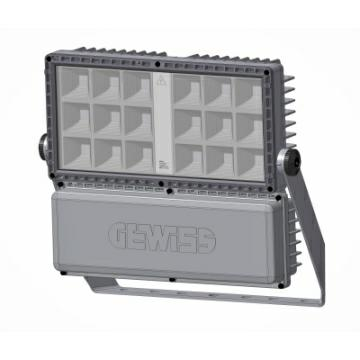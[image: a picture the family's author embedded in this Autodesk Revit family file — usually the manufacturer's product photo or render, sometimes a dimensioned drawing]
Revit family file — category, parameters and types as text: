
# Revit family: Lighting-Floodlights-GEWISS-SMART[PRO]2.0-LED-MEDIUM-POWER_1MODULE_DALI.CLII
name_source: partatom
category: Apparecchi per illuminazione
units: mm (PartAtom-declared; Revit-internal decimal feet)

## family parameters
Condiviso = No
Host = Superficie
Punto di calcolo locali = No
Quota connettore circolare = Usa diametro
Sorgente d'illuminazione = No
Taglio con vuoti quando caricato = No
Tipo di parte = Normale

## types (45) — shared parameters
Applicazione = Indoor / Outdoor
Body = Die-cast aluminium -
Catalogue = LIGHTING
Classification: = -
Colour = Graphite grey
Colour : = Polyester powder coated
Context = Sport, Big Areas
Control System = DALI
DIN 18032-3 certification = Yes
Device with reduced surface temperature = Yes
Driver = Included
Driver Box = Built-in
Eletrical and lighting features = -
External screw = Stainless steel
Fixing = Bracket
GW - Codice Electrocod = 2424
Gasket = Anti-aging silicone
General information = -
Glow Wire Test : = -
IDF = d05ed8b5-b81d-4cb0-8872-352464a63a3f
IDT = 44936a2a5e034791af2c92c80339c9aa
IP degree = IP66
Immagine tipo = SMARTPRO20_1M.jpg
Installationa and maintenance = -
Insulation class = II
LED Maintenance = Not available
Lifetime = L90B10 (Tq+25°C) - 50000h L90B10 (Tq+50°C) = 32000h L80B10 (Tq+25°C) - 110000h
Locking Hook = Hexagonal metric screws
Luminaire = LED luminaire with small,mid and high lumen power
Materials = -
Maximum surface exposed to the wind : = 0,085 m2
Mouting and installation = High-mast lighting - Wall mounting - Ground mouting
Operating temperature : = -30 +50 °C
Optic Maintenance = Not available
Optic and illuminating features = -
Overvoltage protection = DM 6 kV / CM 10 kV
Photobiological Risk Class = -
Produttore = GEWISS S.p.A.
Prospetto di default = 1219 mm
Rated frequency (Hz) = 50 / 60
SEO = Floodlight
Shield type = Flat tempered glass 4mm
Shock resistance = IK08
Standard- = EN60598-1; EN60598-2-5; EN60598-2-24; IEC 62778; IEC62471; EN13201
Standards and approvals = -
Stocking temperature = -
Supply voltage = 220 - 240 V
System power = 165W
Technical sheet = https://www.gewiss.com
Tilt- = Rotation on bracket with integrated goniometer
Type of light source = LED - Not replaceable
URL = https://www.gewiss.com
Unique digital code (Datamatrix) = Currently not present
Version file RFA = 20.11
Warranty = 5 years
Weight (kg): = 5,7
Wiring = Watertight connector

## per-type parameters (varying)
| type | Color Rendering Index | Colour temperature | Descrizione | Efficiency (lm/W) | IPEA | Lumen output (lm) | Modello | Optic | Optic : | Standard Deviation Colour Matching | Unified Glare Rating | Versions |
| GWP2174LB - SMARTPRO2.0 1M 4000K CRI70 C2 DALI CL2 | CRI-70 | 4000K | SMARTPRO2.0 1M 4000K CRI70 C2 DALI CL2 | 121 | ROAD = A ++ // LARGE AREAS = A5 + // CYCLOPEDONALS = A ++ // GREEN AREAS = A ++ // HISTORICAL CENTER = A7 + // OTHER = A7 + | 20000 | GWP2174LB | C2 - Circular 25° | Polished quartz and metallized PC HT reflector | SDCM = 5 | G*6 - ULOR = 0 | 4000K natural light |
| GWP2183BB - SMARTPRO2.0 1M 3000K CRI80 S2 DALI CL2 | CRI-80 | 3000K | SMARTPRO2.0 1M 3000K CRI80 S2 DALI CL2 | 107 | ROAD = A // LARGE AREAS = A3 + // CYCLOPEDONALS = A + // GREEN AREAS = A + // HISTORICAL CENTER = A5 + // OTHER = A5 + | 17600 | GWP2183BB | S2 - Symmetric Medium | Polished anodised aluminum reflector with 99.99% pure aluminum | SDCM = 3 | G*6 - ULOR = 0 | 3000K warm light |
| GWP2174CB - SMARTPRO2.0 1M 4000K CRI70 A1 DALI CL2 | CRI-70 | 4000K | SMARTPRO2.0 1M 4000K CRI70 A1 DALI CL2 | 116 | ROAD = A + // LARGE AREAS = A5 + // CYCLOPEDONALS = A ++ // GREEN AREAS = A ++ // HISTORICAL CENTER = A6 + // OTHER = A6 + | 19100 | GWP2174CB | A1 - Asymmetrical Wide | Polished quartz and metallized PC HT reflector | SDCM = 5 | G*4 - ULOR = 0 | 4000K natural light |
| GWP2184MB - SMARTPRO2.0 1M 4000K CRI80 C1 DALI CL2 | CRI-80 | 4000K | SMARTPRO2.0 1M 4000K CRI80 C1 DALI CL2 | 113 | - | 18700 | GWP2184MB | C1 - Circular 30° | Polished quartz and metallized PC HT reflector | SDCM = 3 | G*6 - ULOR = 0 | 4000K natural light |
| GWP2174GB - SMARTPRO2.0 1M 4000K CRI70 C4 DALI CL2 | CRI-70 | 4000K | SMARTPRO2.0 1M 4000K CRI70 C4 DALI CL2 | 124 | ROAD = A ++ // LARGE AREAS = A6 + // CYCLOPEDONALS = A3 + // GREEN AREAS = A3 + // HISTORICAL CENTER = A8 + // OTHER = A8 + | 20500 | GWP2174GB | C4 - Circular 15° | Polished quartz and metallized PC HT reflector | SDCM = 5 | G*6 - ULOR = 0 | 4000K natural light |
| GWP2173FB - SMARTPRO2.0 1M 3000K CRI70 A2 DALI CL2 | CRI-70 | 3000K | SMARTPRO2.0 1M 3000K CRI70 A2 DALI CL2 | 93 | ROAD = B // LARGE AREAS = A + // CYCLOPEDONALS = B // GREEN AREAS = B // HISTORICAL CENTER = A3 + // OTHER = A3 + | 15300 | GWP2173FB | A2 - Asymmetrical Medium | Polished anodised aluminum reflector with 99.99% pure aluminum | SDCM = 5 | G*3 - ULOR = 0 | 3000K warm light |
| GWP2174BB - SMARTPRO2.0 1M 4000K CRI70 S2 DALI CL2 | CRI-70 | 4000K | SMARTPRO2.0 1M 4000K CRI70 S2 DALI CL2 | 123 | ROAD = A ++ // LARGE AREAS = A6 + // CYCLOPEDONALS = A3 + // GREEN AREAS = A3 + // HISTORICAL CENTER = A7 + // OTHER = A7 + | 20300 | GWP2174BB | S2 - Symmetric Medium | Polished anodised aluminum reflector with 99.99% pure aluminum | SDCM = 5 | G*6 - ULOR = 0 | 4000K natural light |
| GWP2175LB - SMARTPRO2.0 1M 5700K CRI70 C2 DALI CL2 | CRI-70 | 5700K | SMARTPRO2.0 1M 5700K CRI70 C2 DALI CL2 | 121 | ROAD = A ++ // LARGE AREAS = A5 + // CYCLOPEDONALS = A ++ // GREEN AREAS = A ++ // HISTORICAL CENTER = A7 + // OTHER = A7 + | 20000 | GWP2175LB | C2 - Circular 25° | Polished quartz and metallized PC HT reflector | SDCM = 5 | G*6 - ULOR = 0 | 5700K cold light |
| GWP2183MB - SMARTPRO2.0 1M 3000K CRI80 C1 DALI CL2 | CRI-80 | 3000K | SMARTPRO2.0 1M 3000K CRI80 C1 DALI CL2 | 105 | ROAD = A // LARGE AREAS = A3 + // CYCLOPEDONALS = A + // GREEN AREAS = A + // HISTORICAL CENTER = A5 + // OTHER = A5 + | 17400 | GWP2183MB | C1 - Circular 30° | Polished quartz and metallized PC HT reflector | SDCM = 3 | G*6 - ULOR = 0 | 3000K warm light |
| GWP2175NB - SMARTPRO2.0 1M 5700K CRI70 A3 DALI CL2 | CRI-70 | 5700K | SMARTPRO2.0 1M 5700K CRI70 A3 DALI CL2 | 114 | - | 18800 | GWP2175NB | A3 - Assymetric Narrow | Polished anodised aluminum reflector with 99.99% pure aluminum | SDCM = 5 | G*6 - ULOR = 0 | 5700K cold light |
| GWP2174AB - SMARTPRO2.0 1M 4000K CRI70 S1 DALI CL2 | CRI-70 | 4000K | SMARTPRO2.0 1M 4000K CRI70 S1 DALI CL2 | 119 | ROAD = A ++ // LARGE AREAS = A5 + // CYCLOPEDONALS = A ++ // GREEN AREAS = A ++ // HISTORICAL CENTER = A7 + // OTHER = A7 + | 19600 | GWP2174AB | S1 - Symmetric Wide | Polished quartz and metallized PC HT reflector | SDCM = 5 | G*6 - ULOR = 0 | 4000K natural light |
| GWP2184HB - SMARTPRO2.0 1M 4000K CRI80 C3 DALI CL2 | CRI-80 | 4000K | SMARTPRO2.0 1M 4000K CRI80 C3 DALI CL2 | 116 | ROAD = A + // LARGE AREAS = A5 + // CYCLOPEDONALS = A ++ // GREEN AREAS = A ++ // HISTORICAL CENTER = A6 + // OTHER = A6 + | 19100 | GWP2184HB | C3 - Circular 20° | Polished quartz and metallized PC HT reflector | SDCM = 3 | G*6 - ULOR = 0 | 4000K natural light |
| GWP2174MB - SMARTPRO2.0 1M 4000K CRI70 C1 DALI CL2 | CRI-70 | 4000K | SMARTPRO2.0 1M 4000K CRI70 C1 DALI CL2 | 121 | ROAD = A ++ // LARGE AREAS = A5 + // CYCLOPEDONALS = A ++ // GREEN AREAS = A ++ // HISTORICAL CENTER = A7 + // OTHER = A7 + | 20000 | GWP2174MB | C1 - Circular 30° | Polished quartz and metallized PC HT reflector | SDCM = 5 | G*6 - ULOR = 0 | 4000K natural light |
| GWP2175MB - SMARTPRO2.0 1M 5700K CRI70 C1 DALI CL2 | CRI-70 | 5700K | SMARTPRO2.0 1M 5700K CRI70 C1 DALI CL2 | 121 | ROAD = A ++ // LARGE AREAS = A5 + // CYCLOPEDONALS = A ++ // GREEN AREAS = A ++ // HISTORICAL CENTER = A7 + // OTHER = A7 + | 20000 | GWP2175MB | C1 - Circular 30° | Polished quartz and metallized PC HT reflector | SDCM = 5 | G*6 - ULOR = 0 | 5700K cold light |
| GWP2184LB - SMARTPRO2.0 1M 4000K CRI80 C2 DALI CL2 | CRI-80 | 4000K | SMARTPRO2.0 1M 4000K CRI80 C2 DALI CL2 | 113 | - | 18700 | GWP2184LB | C2 - Circular 25° | Polished quartz and metallized PC HT reflector | SDCM = 3 | G*6 - ULOR = 0 | 4000K natural light |
| GWP2183LB - SMARTPRO2.0 1M 3000K CRI80 C2 DALI CL2 | CRI-80 | 3000K | SMARTPRO2.0 1M 3000K CRI80 C2 DALI CL2 | 105 | ROAD = A // LARGE AREAS = A3 + // CYCLOPEDONALS = A + // GREEN AREAS = A + // HISTORICAL CENTER = A5 + // OTHER = A5 + | 17400 | GWP2183LB | C2 - Circular 25° | Polished quartz and metallized PC HT reflector | SDCM = 3 | G*6 - ULOR = 0 | 3000K warm light |
| GWP2175GB - SMARTPRO2.0 1M 5700K CRI70 C4 DALI CL2 | CRI-70 | 5700K | SMARTPRO2.0 1M 5700K CRI70 C4 DALI CL2 | 124 | ROAD = A ++ // LARGE AREAS = A6 + // CYCLOPEDONALS = A3 + // GREEN AREAS = A3 + // HISTORICAL CENTER = A8 + // OTHER = A8 + | 20500 | GWP2175GB | C4 - Circular 15° | Polished quartz and metallized PC HT reflector | SDCM = 5 | G*6 - ULOR = 0 | 5700K cold light |
| GWP2173BB - SMARTPRO2.0 1M 3000K CRI70 S2 DALI CL2 | CRI-70 | 3000K | SMARTPRO2.0 1M 3000K CRI70 S2 DALI CL2 | 115 | ROAD = A + // LARGE AREAS = A5 + // CYCLOPEDONALS = A ++ // GREEN AREAS = A ++ // HISTORICAL CENTER = A6 + // OTHER = A6 + | 19000 | GWP2173BB | S2 - Symmetric Medium | Polished anodised aluminum reflector with 99.99% pure aluminum | SDCM = 5 | G*6 - ULOR = 0 | 3000K warm light |
| GWP2183NB - SMARTPRO2.0 1M 3000K CRI80 A3 DALI CL2 | CRI-80 | 3000K | SMARTPRO2.0 1M 3000K CRI80 A3 DALI CL2 | 99 | ROAD = A // LARGE AREAS = A ++ // CYCLOPEDONALS = A // GREEN AREAS = A // HISTORICAL CENTER = A4 + // OTHER = A4 + | 16300 | GWP2183NB | A3 - Assymetric Narrow | Polished anodised aluminum reflector with 99.99% pure aluminum | SDCM = 3 | G*6 - ULOR = 0 | 3000K warm light |
| GWP2173LB - SMARTPRO2.0 1M 3000K CRI70 C2 DALI CL2 | CRI-70 | 3000K | SMARTPRO2.0 1M 3000K CRI70 C2 DALI CL2 | 113 | - | 18700 | GWP2173LB | C2 - Circular 25° | Polished quartz and metallized PC HT reflector | SDCM = 5 | G*6 - ULOR = 0 | 3000K warm light |
| GWP2183GB - SMARTPRO2.0 1M 3000K CRI80 C4 DALI CL2 | CRI-80 | 3000K | SMARTPRO2.0 1M 3000K CRI80 C4 DALI CL2 | 108 | ROAD = A + // LARGE AREAS = A3 + // CYCLOPEDONALS = A + // GREEN AREAS = A + // HISTORICAL CENTER = A5 + // OTHER = A5 + | 17800 | GWP2183GB | C4 - Circular 15° | Polished quartz and metallized PC HT reflector | SDCM = 3 | G*6 - ULOR = 0 | 3000K warm light |
| GWP2183CB - SMARTPRO2.0 1M 3000K CRI80 A1 DALI CL2 | CRI-80 | 3000K | SMARTPRO2.0 1M 3000K CRI80 A1 DALI CL2 | 100 | ROAD = A // LARGE AREAS = A ++ // CYCLOPEDONALS = A // GREEN AREAS = A // HISTORICAL CENTER = A4 + // OTHER = A4 + | 16500 | GWP2183CB | A1 - Asymmetrical Wide | Polished quartz and metallized PC HT reflector | SDCM = 3 | G*4 - ULOR = 0 | 3000K warm light |
| GWP2174FB - SMARTPRO2.0 1M 4000K CRI70 A2 DALI CL2 | CRI-70 | 4000K | SMARTPRO2.0 1M 4000K CRI70 A2 DALI CL2 | 99 | ROAD = A // LARGE AREAS = A ++ // CYCLOPEDONALS = A // GREEN AREAS = A // HISTORICAL CENTER = A4 + // OTHER = A4 + | 16400 | GWP2174FB | A2 - Asymmetrical Medium | Polished anodised aluminum reflector with 99.99% pure aluminum | SDCM = 5 | G*3 - ULOR = 0 | 4000K natural light |
| GWP2175BB - SMARTPRO2.0 1M 5700K CRI70 S2 DALI CL2 | CRI-70 | 5700K | SMARTPRO2.0 1M 5700K CRI70 S2 DALI CL2 | 123 | ROAD = A ++ // LARGE AREAS = A6 + // CYCLOPEDONALS = A3 + // GREEN AREAS = A3 + // HISTORICAL CENTER = A7 + // OTHER = A7 + | 20300 | GWP2175BB | S2 - Symmetric Medium | Polished anodised aluminum reflector with 99.99% pure aluminum | SDCM = 5 | G*6 - ULOR = 0 | 5700K cold light |
| GWP2175CB - SMARTPRO2.0 1M 5700K CRI70 A1 DALI CL2 | CRI-70 | 5700K | SMARTPRO2.0 1M 5700K CRI70 A1 DALI CL2 | 116 | ROAD = A + // LARGE AREAS = A5 + // CYCLOPEDONALS = A ++ // GREEN AREAS = A ++ // HISTORICAL CENTER = A6 + // OTHER = A6 + | 19100 | GWP2175CB | A1 - Asymmetrical Wide | Polished quartz and metallized PC HT reflector | SDCM = 5 | G*4 - ULOR = 0 | 5700K cold light |
| GWP2173NB - SMARTPRO2.0 1M 3000K CRI70 A3 DALI CL2 | CRI-70 | 3000K | SMARTPRO2.0 1M 3000K CRI70 A3 DALI CL2 | 107 | ROAD = A // LARGE AREAS = A3 + // CYCLOPEDONALS = A + // GREEN AREAS = A + // HISTORICAL CENTER = A5 + // OTHER = A5 + | 17600 | GWP2173NB | A3 - Assymetric Narrow | Polished anodised aluminum reflector with 99.99% pure aluminum | SDCM = 5 | G*6 - ULOR = 0 | 3000K warm light |
| GWP2184CB - SMARTPRO2.0 1M 4000K CRI80 A1 DALI CL2 | CRI-80 | 4000K | SMARTPRO2.0 1M 4000K CRI80 A1 DALI CL2 | 108 | ROAD = A + // LARGE AREAS = A3 + // CYCLOPEDONALS = A + // GREEN AREAS = A + // HISTORICAL CENTER = A5 + // OTHER = A5 + | 17800 | GWP2184CB | A1 - Asymmetrical Wide | Polished quartz and metallized PC HT reflector | SDCM = 3 | G*4 - ULOR = 0 | 4000K natural light |
| GWP2174HB - SMARTPRO2.0 1M 4000K CRI70 C3 DALI CL2 | CRI-70 | 4000K | SMARTPRO2.0 1M 4000K CRI70 C3 DALI CL2 | 124 | ROAD = A ++ // LARGE AREAS = A6 + // CYCLOPEDONALS = A3 + // GREEN AREAS = A3 + // HISTORICAL CENTER = A8 + // OTHER = A8 + | 20500 | GWP2174HB | C3 - Circular 20° | Polished quartz and metallized PC HT reflector | SDCM = 5 | G*6 - ULOR = 0 | 4000K natural light |
| GWP2183AB - SMARTPRO2.0 1M 3000K CRI80 S1 DALI CL2 | CRI-80 | 3000K | SMARTPRO2.0 1M 3000K CRI80 S1 DALI CL2 | 103 | ROAD = A // LARGE AREAS = A3 + // CYCLOPEDONALS = A // GREEN AREAS = A // HISTORICAL CENTER = A4 + // OTHER = A4 + | 17000 | GWP2183AB | S1 - Symmetric Wide | Polished quartz and metallized PC HT reflector | SDCM = 3 | G*6 - ULOR = 0 | 3000K warm light |
| GWP2175HB - SMARTPRO2.0 1M 5700K CRI70 C3 DALI CL2 | CRI-70 | 5700K | SMARTPRO2.0 1M 5700K CRI70 C3 DALI CL2 | 124 | ROAD = A ++ // LARGE AREAS = A6 + // CYCLOPEDONALS = A3 + // GREEN AREAS = A3 + // HISTORICAL CENTER = A8 + // OTHER = A8 + | 20500 | GWP2175HB | C3 - Circular 20° | Polished quartz and metallized PC HT reflector | SDCM = 5 | G*6 - ULOR = 0 | 5700K cold light |
| GWP2175FB - SMARTPRO2.0 1M 5700K CRI70 A2 DALI CL2 | CRI-70 | 5700K | SMARTPRO2.0 1M 5700K CRI70 A2 DALI CL2 | 99 | ROAD = A // LARGE AREAS = A ++ // CYCLOPEDONALS = A // GREEN AREAS = A // HISTORICAL CENTER = A4 + // OTHER = A4 + | 16400 | GWP2175FB | A2 - Asymmetrical Medium | Polished anodised aluminum reflector with 99.99% pure aluminum | SDCM = 5 | G*3 - ULOR = 0 | 5700K cold light |
| GWP2184NB - SMARTPRO2.0 1M 4000K CRI80 A3 DALI CL2 | CRI-80 | 4000K | SMARTPRO2.0 1M 4000K CRI80 A3 DALI CL2 | 107 | ROAD = A // LARGE AREAS = A3 + // CYCLOPEDONALS = A + // GREEN AREAS = A + // HISTORICAL CENTER = A5 + // OTHER = A5 + | 17600 | GWP2184NB | A3 - Assymetric Narrow | Polished anodised aluminum reflector with 99.99% pure aluminum | SDCM = 3 | G*6 - ULOR = 0 | 4000K natural light |
| GWP2173CB - SMARTPRO2.0 1M 3000K CRI70 A1 DALI CL2 | CRI-70 | 3000K | SMARTPRO2.0 1M 3000K CRI70 A1 DALI CL2 | 108 | ROAD = A + // LARGE AREAS = A3 + // CYCLOPEDONALS = A + // GREEN AREAS = A + // HISTORICAL CENTER = A5 + // OTHER = A5 + | 17800 | GWP2173CB | A1 - Asymmetrical Wide | Polished quartz and metallized PC HT reflector | SDCM = 5 | G*4 - ULOR = 0 | 3000K warm light |
| GWP2173HB - SMARTPRO2.0 1M 3000K CRI70 C3 DALI CL2 | CRI-70 | 3000K | SMARTPRO2.0 1M 3000K CRI70 C3 DALI CL2 | 116 | ROAD = A + // LARGE AREAS = A5 + // CYCLOPEDONALS = A ++ // GREEN AREAS = A ++ // HISTORICAL CENTER = A6 + // OTHER = A6 + | 19100 | GWP2173HB | C3 - Circular 20° | Polished quartz and metallized PC HT reflector | SDCM = 5 | G*6 - ULOR = 0 | 3000K warm light |
| GWP2175AB - SMARTPRO2.0 1M 5700K CRI70 S1 DALI CL2 | CRI-70 | 5700K | SMARTPRO2.0 1M 5700K CRI70 S1 DALI CL2 | 119 | ROAD = A ++ // LARGE AREAS = A5 + // CYCLOPEDONALS = A ++ // GREEN AREAS = A ++ // HISTORICAL CENTER = A7 + // OTHER = A7 + | 19600 | GWP2175AB | S1 - Symmetric Wide | Polished quartz and metallized PC HT reflector | SDCM = 5 | G*6 - ULOR = 0 | 5700K cold light |
| GWP2184BB - SMARTPRO2.0 1M 4000K CRI80 S2 DALI CL2 | CRI-80 | 4000K | SMARTPRO2.0 1M 4000K CRI80 S2 DALI CL2 | 115 | ROAD = A + // LARGE AREAS = A5 + // CYCLOPEDONALS = A ++ // GREEN AREAS = A ++ // HISTORICAL CENTER = A6 + // OTHER = A6 + | 19000 | GWP2184BB | S2 - Symmetric Medium | Polished anodised aluminum reflector with 99.99% pure aluminum | SDCM = 3 | G*6 - ULOR = 0 | 4000K natural light |
| GWP2173GB - SMARTPRO2.0 1M 3000K CRI70 C4 DALI CL2 | CRI-70 | 3000K | SMARTPRO2.0 1M 3000K CRI70 C4 DALI CL2 | 116 | ROAD = A + // LARGE AREAS = A5 + // CYCLOPEDONALS = A ++ // GREEN AREAS = A ++ // HISTORICAL CENTER = A6 + // OTHER = A6 + | 19100 | GWP2173GB | C4 - Circular 15° | Polished quartz and metallized PC HT reflector | SDCM = 5 | G*6 - ULOR = 0 | 3000K warm light |
| GWP2173AB - SMARTPRO2.0 1M 3000K CRI70 S1 DALI CL2 | CRI-70 | 3000K | SMARTPRO2.0 1M 3000K CRI70 S1 DALI CL2 | 111 | - | 18300 | GWP2173AB | S1 - Symmetric Wide | Polished quartz and metallized PC HT reflector | SDCM = 5 | G*6 - ULOR = 0 | 3000K warm light |
| GWP2174NB - SMARTPRO2.0 1M 4000K CRI70 A3 DALI CL2 | CRI-70 | 4000K | SMARTPRO2.0 1M 4000K CRI70 A3 DALI CL2 | 114 | - | 18800 | GWP2174NB | A3 - Assymetric Narrow | Polished anodised aluminum reflector with 99.99% pure aluminum | SDCM = 5 | G*6 - ULOR = 0 | 4000K natural light |
| GWP2173MB - SMARTPRO2.0 1M 3000K CRI70 C1 DALI CL2 | CRI-70 | 3000K | SMARTPRO2.0 1M 3000K CRI70 C1 DALI CL2 | 113 | - | 18700 | GWP2173MB | C1 - Circular 30° | Polished quartz and metallized PC HT reflector | SDCM = 5 | G*6 - ULOR = 0 | 3000K warm light |
| GWP2184GB - SMARTPRO2.0 1M 4000K CRI80 C4 DALI CL2 | CRI-80 | 4000K | SMARTPRO2.0 1M 4000K CRI80 C4 DALI CL2 | 116 | ROAD = A + // LARGE AREAS = A5 + // CYCLOPEDONALS = A ++ // GREEN AREAS = A ++ // HISTORICAL CENTER = A6 + // OTHER = A6 + | 19100 | GWP2184GB | C4 - Circular 15° | Polished quartz and metallized PC HT reflector | SDCM = 3 | G*6 - ULOR = 0 | 4000K natural light |
| GWP2183HB - SMARTPRO2.0 1M 3000K CRI80 C3 DALI CL2 | CRI-80 | 3000K | SMARTPRO2.0 1M 3000K CRI80 C3 DALI CL2 | 108 | ROAD = A + // LARGE AREAS = A3 + // CYCLOPEDONALS = A + // GREEN AREAS = A + // HISTORICAL CENTER = A5 + // OTHER = A5 + | 17800 | GWP2183HB | C3 - Circular 20° | Polished quartz and metallized PC HT reflector | SDCM = 3 | G*6 - ULOR = 0 | 3000K warm light |
| GWP2183FB - SMARTPRO2.0 1M 3000K CRI80 A2 DALI CL2 | CRI-80 | 3000K | SMARTPRO2.0 1M 3000K CRI80 A2 DALI CL2 | 86 | ROAD = C // LARGE AREAS = A + // CYCLOPEDONALS = C // GREEN AREAS = C // HISTORICAL CENTER = A ++ // OTHER = A ++ | 14200 | GWP2183FB | A2 - Asymmetrical Medium | Polished anodised aluminum reflector with 99.99% pure aluminum | SDCM = 3 | G*3 - ULOR = 0 | 3000K warm light |
| GWP2184AB - SMARTPRO2.0 1M 4000K CRI80 S1 DALI CL2 | CRI-80 | 4000K | SMARTPRO2.0 1M 4000K CRI80 S1 DALI CL2 | 111 | - | 18300 | GWP2184AB | S1 - Symmetric Wide | Polished quartz and metallized PC HT reflector | SDCM = 3 | G*6 - ULOR = 0 | 4000K natural light |
| GWP2184FB - SMARTPRO2.0 1M 4000K CRI80 A2 DALI CL2 | CRI-80 | 4000K | SMARTPRO2.0 1M 4000K CRI80 A2 DALI CL2 | 93 | ROAD = B // LARGE AREAS = A + // CYCLOPEDONALS = B // GREEN AREAS = B // HISTORICAL CENTER = A3 + // OTHER = A3 + | 15300 | GWP2184FB | A2 - Asymmetrical Medium | Polished anodised aluminum reflector with 99.99% pure aluminum | SDCM = 3 | G*3 - ULOR = 0 | 4000K natural light |

## geometry (parser evidence)
native form markers: Blend x4
no freeform markers — native parametric forms only
